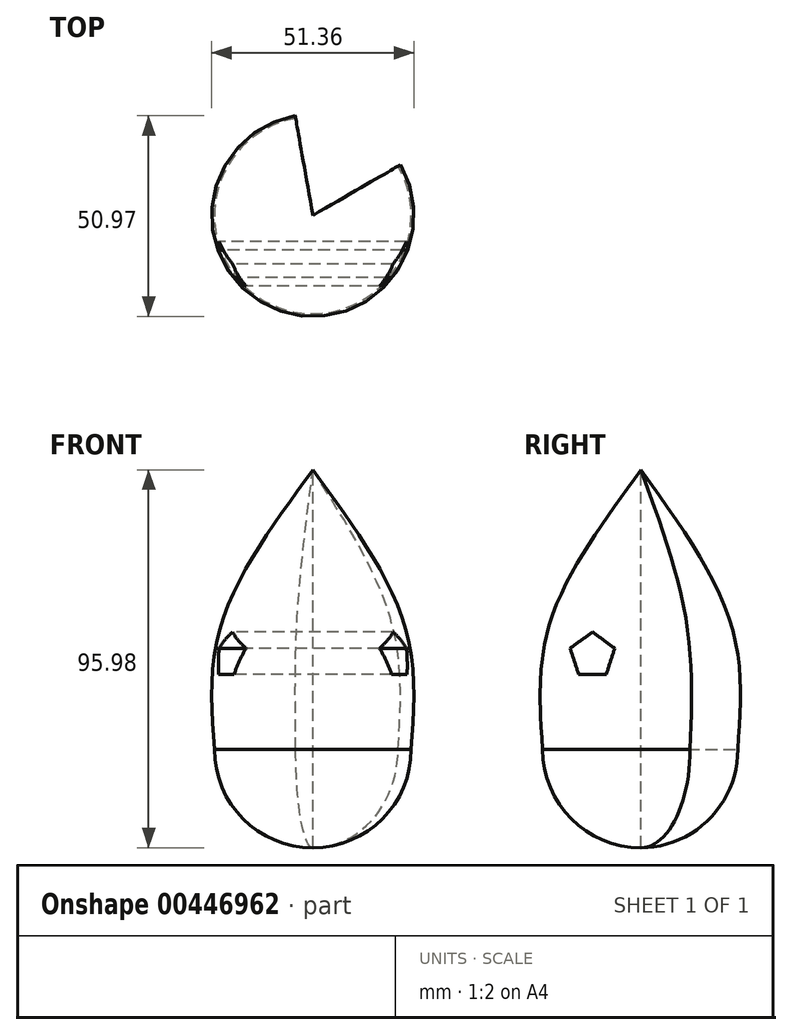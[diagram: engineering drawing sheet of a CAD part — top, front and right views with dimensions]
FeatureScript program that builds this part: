
annotation { "Feature Type Name" : "Feature", "Feature Type Description" : "" }
export const myFeature = defineFeature(function(context is Context, id is Id, definition is map)
    precondition{}
    {
        {
            var Q0;
            Q0=qCreatedBy(makeId("Front.planeOp"),FACE);
            var sketch = newSketch(context, id + "F0", { "sketchPlane" : qUnion([Q0])});
            skCircle(sketch, "E0", {"center": v(0, 0) * mm, "radius": 25 * mm});
            skFitSpline(sketch, "E1", {"points": [v(25, 0) * mm, v(23.3, 31.6) * mm, v(0, 70.98) * mm], "startDerivative": vector(5.1, 69.04) * mm, "endDerivative": vector(-53.32, 72.81) * mm});
            skFitSpline(sketch, "E2.MirrorCS", {"points": [v(-25, 0) * mm, v(-23.3, 31.6) * mm, v(0, 70.98) * mm], "startDerivative": vector(-5.1, 69.04) * mm, "endDerivative": vector(53.32, 72.81) * mm});
            skLineSegment(sketch, "E3", {"start": v(-22.91, 10) * mm, "end": v(22.91, 10) * mm, "construction": true});
            skLineSegment(sketch, "E4", {"start": v(0, -25) * mm, "end": v(0, 70.98) * mm});
            skSolve(sketch);
        }
        {
            var Q0;
            {var subQ0=sQuery(id+"F0.wireOp",EDGE,"E1");Q0=makeQuery(id+"F0.imprint","IMPRINT",FACE,{"disambiguationData":[TD([[makeQuery(id+"F0.imprint","IMPRINT",EDGE,{"derivedFrom":subQ0}),1.0]])]});}
            var Q1;
            {var subQ0=sQuery(id+"F0.wireOp",EDGE,"E0");var subQ1=makeQuery(id+"F0.imprint","INTERSECT",VERTEX,{"derivedFrom":[subQ0,sQuery(id+"F0.wireOp",EDGE,"E1")]});Q1=makeQuery(id+"F0.imprint","IMPRINT",FACE,{"disambiguationData":[TD([[makeQuery(id+"F0.imprint","IMPRINT",EDGE,{"disambiguationData":[TD([[subQ1,-1.0]])],"derivedFrom":subQ0}),1.0]])]});}
            var Q2;
            Q2=sQuery(id+"F0.wireOp",EDGE,"E4");
            revolve(context, id + "F1", {"entities" : qUnion([Q0, Q1]), "axis" : qUnion([Q2]), "revolveType" : RevolveType.TWO_DIRECTIONS, "angle" : 30 * degree, "angleBack" : 100 * degree});
        }
        {
            var Q0;
            Q0=qCreatedBy(makeId("Right.planeOp"),FACE);
            cPlane(context, id + "F2", {"entities" : qUnion([Q0]), "cplaneType" : CPlaneType.OFFSET, "offset" : 50 * mm, "oppositeDirection" : true, "width" : 150 * mm, "height" : 150 * mm});
        }
        {
            var Q0;
            Q0=qCreatedBy(id+"F2.planeOp",FACE);
            var sketch = newSketch(context, id + "F3", { "sketchPlane" : qUnion([Q0])});
            skFitSpline(sketch, "E5", {"points": [v(-25, 0) * mm, v(-25.77, 10.45) * mm, v(-27.48, 33.46) * mm, v(-9.7, 57.73) * mm, v(0, 70.98) * mm]});
            skLineSegment(sketch, "E6.0.0", {"start": v(-25, 0) * mm, "end": v(24.62, 0) * mm});
            skEllipticalArc(sketch, "E6.0.1", {});
            skEllipticalArc(sketch, "E6.0.2", {});
            skFitSpline(sketch, "E7", {"points": [v(-25, 0) * mm, v(-25.77, 10.45) * mm, v(-27.48, 33.46) * mm, v(-9.7, 57.73) * mm, v(0, 70.98) * mm]});
            skCircle(sketch, "E8.cCircle", {"center": v(-12.32, 23.84) * mm, "radius": 4.82 * mm, "construction": true});
            skLineSegment(sketch, "E8.0", {"start": v(-8.82, 19.02) * mm, "end": v(-15.82, 19.02) * mm});
            skLineSegment(sketch, "E8.1", {"start": v(-15.82, 19.02) * mm, "end": v(-17.99, 25.68) * mm});
            skLineSegment(sketch, "E8.2", {"start": v(-17.99, 25.68) * mm, "end": v(-12.32, 29.8) * mm});
            skLineSegment(sketch, "E8.3", {"start": v(-12.32, 29.8) * mm, "end": v(-6.65, 25.68) * mm});
            skLineSegment(sketch, "E8.4", {"start": v(-6.65, 25.68) * mm, "end": v(-8.82, 19.02) * mm});
            skPoint(sketch, "E8.0.midPoint", {"position": v(-12.32, 19.02) * mm});
            const initialGuessF3  = {"E6.0.1": [0, 0, 0, 1, 0.025, 0.0246201938253052, 3.141592653589793, 4.71238898038469], "E6.0.2": [0, 0, 0, 1, 0.025, 0.0125, 3.141592653589793, 4.71238898038469]};
            skSetInitialGuess(sketch, initialGuessF3);
            skSolve(sketch);
        }
        {
            var Q0;
            Q0=makeQuery(id+"F3.imprint","IMPRINT",FACE,{"disambiguationData":[TD([[makeQuery(id+"F3.imprint","IMPRINT",EDGE,{"derivedFrom":sQuery(id+"F3.wireOp",EDGE,"E8.0")}),-1.0]])]});
            extrude(context, id + "F4", {"entities" : qUnion([Q0]), "operationType" : NewBodyOperationType.REMOVE, "depth" : 80 * mm});
        }
    });
